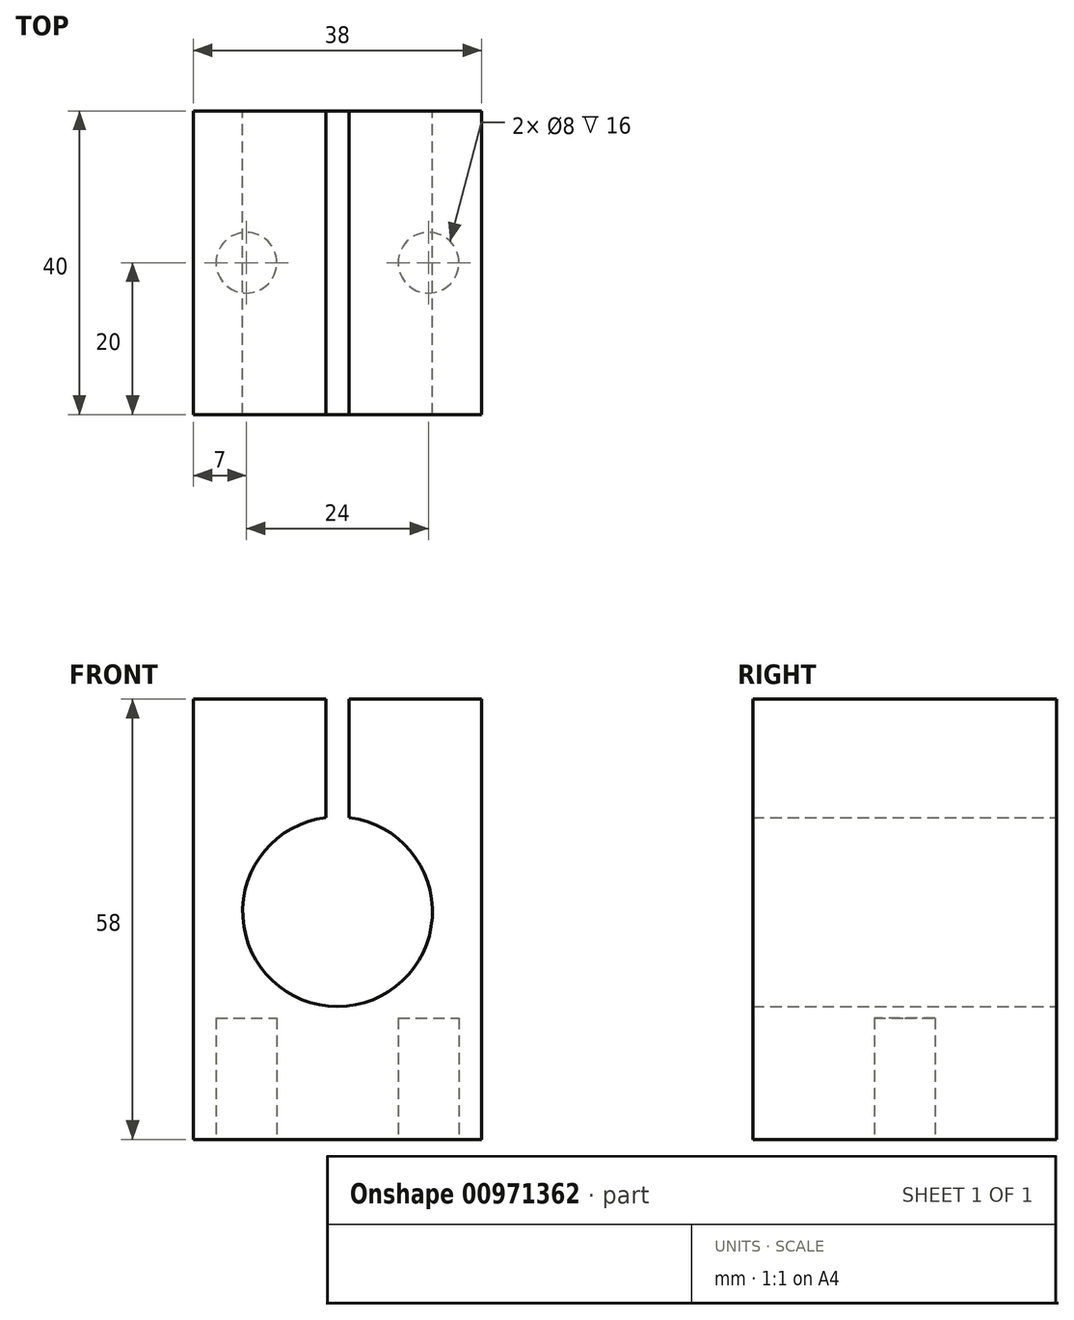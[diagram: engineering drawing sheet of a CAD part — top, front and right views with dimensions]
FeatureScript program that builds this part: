
annotation { "Feature Type Name" : "Feature", "Feature Type Description" : "" }
export const myFeature = defineFeature(function(context is Context, id is Id, definition is map)
    precondition{}
    {
        {
            var Q0;
            Q0=qCreatedBy(makeId("Front.planeOp"),FACE);
            var sketch = newSketch(context, id + "F0", { "sketchPlane" : qUnion([Q0])});
            skLineSegment(sketch, "E0.bottom", {"start": v(19, 29) * mm, "end": v(-19, 29) * mm});
            skLineSegment(sketch, "E0.top", {"start": v(19, -29) * mm, "end": v(-19, -29) * mm});
            skLineSegment(sketch, "E0.left", {"start": v(19, 29) * mm, "end": v(19, -29) * mm});
            skLineSegment(sketch, "E0.right", {"start": v(-19, 29) * mm, "end": v(-19, -29) * mm});
            skPoint(sketch, "E0.middle", {"position": v(0, 0) * mm});
            skLineSegment(sketch, "E1", {"start": v(1.5, 29) * mm, "end": v(1.5, 13.4) * mm, "construction": true});
            skPoint(sketch, "E2.orphan", {"position": v(-1.5, 29) * mm});
            skLineSegment(sketch, "E3", {"start": v(-1.5, 29) * mm, "end": v(-1.5, 13.4) * mm, "construction": true});
            skArc(sketch, "E4", {"start": v(-1.5, 13.4) * mm, "mid": v(0, -11.5) * mm, "end": v(1.5, 13.4) * mm});
            skLineSegment(sketch, "E5", {"start": v(-1.5, 13.4) * mm, "end": v(-1.5, 29) * mm});
            skLineSegment(sketch, "E6", {"start": v(1.5, 13.4) * mm, "end": v(1.5, 29) * mm});
            skPoint(sketch, "E7.start.orphan", {"position": v(-19, 1) * mm});
            skPoint(sketch, "E8.trimOffspring.end.orphan", {"position": v(19, 1) * mm});
            skPoint(sketch, "E9.end.orphan", {"position": v(0, 29) * mm});
            skSolve(sketch);
        }
        {
            var Q0;
            Q0=makeQuery(id+"F0.imprint","IMPRINT",FACE,{"disambiguationData":[TD([[makeQuery(id+"F0.imprint","IMPRINT",EDGE,{"derivedFrom":sQuery(id+"F0.wireOp",EDGE,"E0.top")}),-1.0]])]});
            extrude(context, id + "F1", {"entities" : qUnion([Q0]), "depth" : 40 * mm, "offsetDistance" : 25 * mm});
        }
        {
            var Q0;
            Q0=makeQuery(id+"F1.opExtrude","SWEPT_FACE",FACE,{"disambiguationData":[OSD([sQuery(id+"F0.wireOp",EDGE,"E0.top")])]});
            var sketch = newSketch(context, id + "F2", { "sketchPlane" : qUnion([Q0])});
            skCircle(sketch, "E10", {"center": v(-12, 20) * mm, "radius": 4 * mm});
            skCircle(sketch, "E11", {"center": v(12, 20) * mm, "radius": 4 * mm});
            skPoint(sketch, "E12.orphan", {"position": v(-19, 20) * mm});
            skPoint(sketch, "E13.orphan", {"position": v(-12, 40) * mm});
            skPoint(sketch, "E14.orphan", {"position": v(-12, 0) * mm});
            skPoint(sketch, "E15.orphan", {"position": v(12, 40) * mm});
            skPoint(sketch, "E16.orphan", {"position": v(12, 0) * mm});
            skPoint(sketch, "E17.end.orphan", {"position": v(19, 20) * mm});
            skSolve(sketch);
        }
        {
            var Q0;
            Q0=makeQuery(id+"F2.imprint","IMPRINT",FACE,{"disambiguationData":[TD([[makeQuery(id+"F2.imprint","IMPRINT",EDGE,{"derivedFrom":sQuery(id+"F2.wireOp",EDGE,"E10")}),1.0]])]});
            var Q1;
            Q1=makeQuery(id+"F2.imprint","IMPRINT",FACE,{"disambiguationData":[TD([[makeQuery(id+"F2.imprint","IMPRINT",EDGE,{"derivedFrom":sQuery(id+"F2.wireOp",EDGE,"E11")}),1.0]])]});
            extrude(context, id + "F3", {"entities" : qUnion([Q0, Q1]), "operationType" : NewBodyOperationType.REMOVE, "oppositeDirection" : true, "depth" : 16 * mm, "offsetDistance" : 25 * mm});
        }
    });
